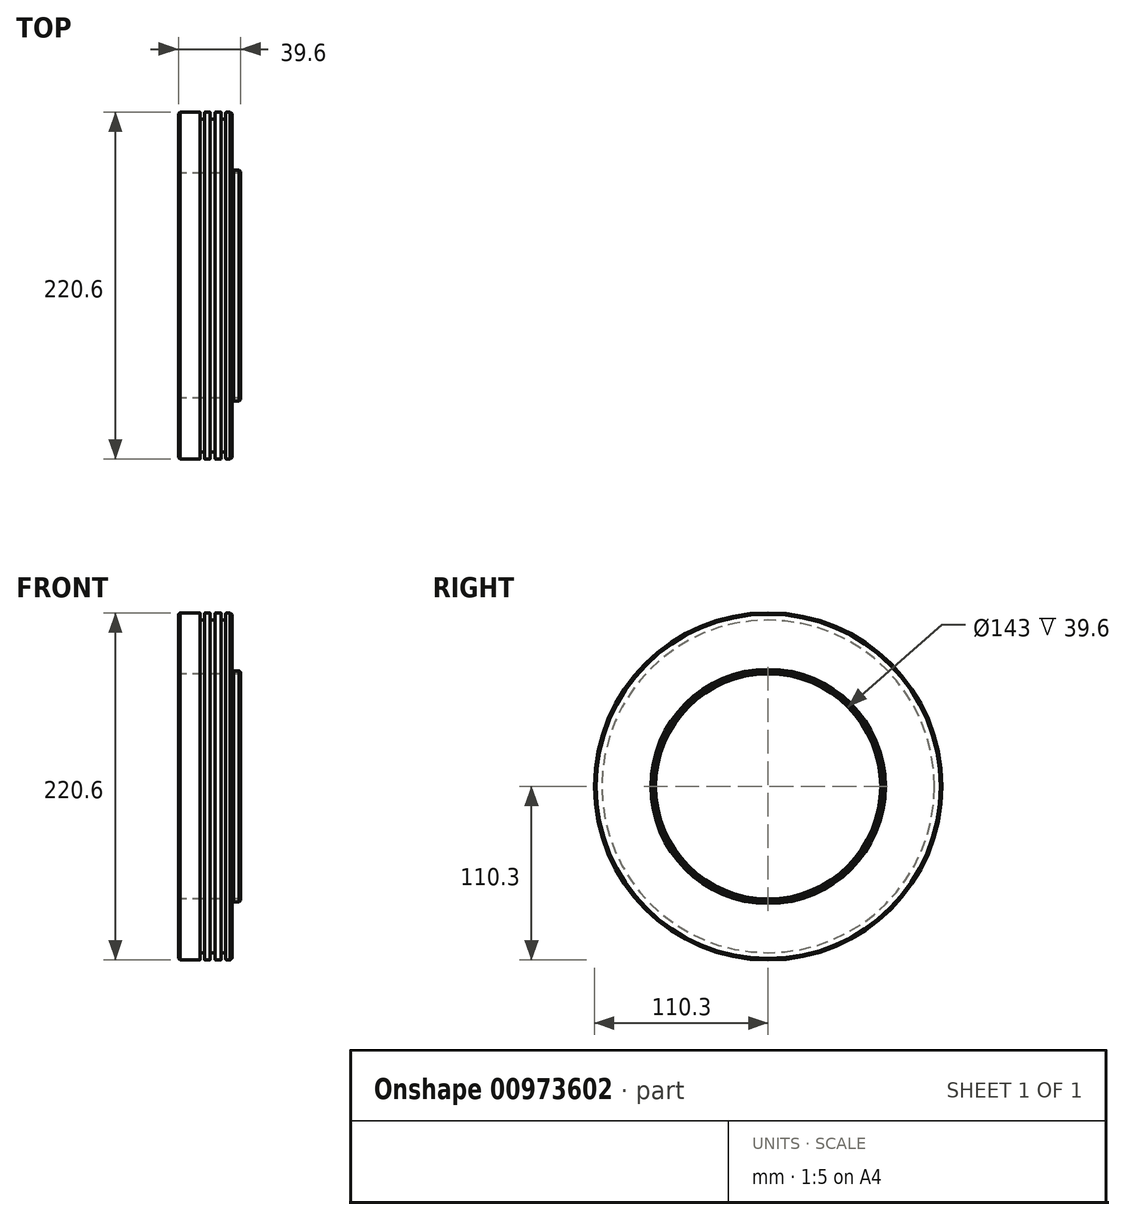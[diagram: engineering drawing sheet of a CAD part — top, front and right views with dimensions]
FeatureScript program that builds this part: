
annotation { "Feature Type Name" : "Feature", "Feature Type Description" : "" }
export const myFeature = defineFeature(function(context is Context, id is Id, definition is map)
    precondition{}
    {
        {
            var Q0;
            Q0=qCreatedBy(makeId("Front.planeOp"),FACE);
            var sketch = newSketch(context, id + "F0", { "sketchPlane" : qUnion([Q0])});
            skLineSegment(sketch, "E0.bottom", {"start": v(0, 0) * mm, "end": v(39.6, 0) * mm});
            skLineSegment(sketch, "E0.top", {"start": v(0, 38.8) * mm, "end": v(13.4, 38.8) * mm});
            skLineSegment(sketch, "E0.left", {"start": v(0, 0) * mm, "end": v(0, 38.8) * mm});
            skLineSegment(sketch, "E0.right", {"start": v(39.6, 0) * mm, "end": v(39.6, 1.92) * mm});
            skLineSegment(sketch, "E1", {"start": v(13.9, 38.3) * mm, "end": v(13.9, 34.62) * mm});
            skLineSegment(sketch, "E2", {"start": v(14.4, 34.12) * mm, "end": v(16.08, 34.12) * mm});
            skLineSegment(sketch, "E3", {"start": v(16.58, 34.62) * mm, "end": v(16.58, 38.3) * mm});
            skLineSegment(sketch, "E4", {"start": v(17.08, 38.8) * mm, "end": v(19.7, 38.8) * mm});
            skLineSegment(sketch, "E5", {"start": v(20.2, 38.3) * mm, "end": v(20.2, 34.62) * mm});
            skLineSegment(sketch, "E6", {"start": v(20.7, 34.12) * mm, "end": v(22.85, 34.12) * mm});
            skLineSegment(sketch, "E7", {"start": v(23.35, 34.62) * mm, "end": v(23.35, 38.3) * mm});
            skLineSegment(sketch, "E8", {"start": v(23.85, 38.8) * mm, "end": v(26.7, 38.8) * mm});
            skLineSegment(sketch, "E9", {"start": v(27.2, 38.3) * mm, "end": v(27.2, 34.62) * mm});
            skLineSegment(sketch, "E10", {"start": v(27.7, 34.12) * mm, "end": v(29.62, 34.12) * mm});
            skLineSegment(sketch, "E11", {"start": v(30.12, 34.62) * mm, "end": v(30.12, 38.3) * mm});
            skLineSegment(sketch, "E12", {"start": v(30.62, 38.8) * mm, "end": v(33.96, 38.8) * mm});
            skLineSegment(sketch, "E13", {"start": v(33.96, 38.8) * mm, "end": v(33.96, 1.92) * mm});
            skLineSegment(sketch, "E14", {"start": v(33.96, 1.92) * mm, "end": v(39.6, 1.92) * mm});
            skLineSegment(sketch, "E15.trimOffspring", {"start": v(30.12, 38.8) * mm, "end": v(33.96, 38.8) * mm});
            skLineSegment(sketch, "E16.trimOffspring", {"start": v(23.35, 38.8) * mm, "end": v(27.2, 38.8) * mm});
            skLineSegment(sketch, "E17.trimOffspring", {"start": v(16.58, 38.8) * mm, "end": v(20.2, 38.8) * mm});
            skLineSegment(sketch, "E18", {"start": v(0, -71.5) * mm, "end": v(42.38, -71.5) * mm, "construction": true});
            skPoint(sketch, "E19.visualSharp", {"position": v(13.9, 34.12) * mm});
            skArc(sketch, "E19.filletArc", {"start": v(13.9, 34.62) * mm, "mid": v(14.04, 34.26) * mm, "end": v(14.4, 34.12) * mm});
            skPoint(sketch, "E20.visualSharp", {"position": v(16.58, 34.12) * mm});
            skArc(sketch, "E20.filletArc", {"start": v(16.08, 34.12) * mm, "mid": v(16.44, 34.26) * mm, "end": v(16.58, 34.62) * mm});
            skPoint(sketch, "E21.visualSharp", {"position": v(16.58, 38.8) * mm});
            skArc(sketch, "E21.filletArc", {"start": v(17.08, 38.8) * mm, "mid": v(16.73, 38.65) * mm, "end": v(16.58, 38.3) * mm});
            skPoint(sketch, "E22.visualSharp", {"position": v(13.9, 38.8) * mm});
            skArc(sketch, "E22.filletArc", {"start": v(13.9, 38.3) * mm, "mid": v(13.75, 38.65) * mm, "end": v(13.4, 38.8) * mm});
            skPoint(sketch, "E23.visualSharp", {"position": v(20.2, 38.8) * mm});
            skArc(sketch, "E23.filletArc", {"start": v(20.2, 38.3) * mm, "mid": v(20.05, 38.65) * mm, "end": v(19.7, 38.8) * mm});
            skPoint(sketch, "E24.visualSharp", {"position": v(20.2, 34.12) * mm});
            skArc(sketch, "E24.filletArc", {"start": v(20.2, 34.62) * mm, "mid": v(20.34, 34.26) * mm, "end": v(20.7, 34.12) * mm});
            skPoint(sketch, "E25.visualSharp", {"position": v(23.35, 34.12) * mm});
            skArc(sketch, "E25.filletArc", {"start": v(22.85, 34.12) * mm, "mid": v(23.2, 34.26) * mm, "end": v(23.35, 34.62) * mm});
            skPoint(sketch, "E26.visualSharp", {"position": v(23.35, 38.8) * mm});
            skArc(sketch, "E26.filletArc", {"start": v(23.85, 38.8) * mm, "mid": v(23.5, 38.65) * mm, "end": v(23.35, 38.3) * mm});
            skPoint(sketch, "E27.visualSharp", {"position": v(27.2, 38.8) * mm});
            skArc(sketch, "E27.filletArc", {"start": v(27.2, 38.3) * mm, "mid": v(27.04, 38.65) * mm, "end": v(26.7, 38.8) * mm});
            skPoint(sketch, "E28.visualSharp", {"position": v(27.2, 34.12) * mm});
            skArc(sketch, "E28.filletArc", {"start": v(27.2, 34.62) * mm, "mid": v(27.34, 34.26) * mm, "end": v(27.7, 34.12) * mm});
            skPoint(sketch, "E29.visualSharp", {"position": v(30.12, 34.12) * mm});
            skArc(sketch, "E29.filletArc", {"start": v(29.62, 34.12) * mm, "mid": v(29.98, 34.26) * mm, "end": v(30.12, 34.62) * mm});
            skPoint(sketch, "E30.visualSharp", {"position": v(30.12, 38.8) * mm});
            skArc(sketch, "E30.filletArc", {"start": v(30.62, 38.8) * mm, "mid": v(30.27, 38.65) * mm, "end": v(30.12, 38.3) * mm});
            skSolve(sketch);
        }
        {
            var Q0;
            Q0=makeQuery(id+"F0.imprint","IMPRINT",FACE,{"disambiguationData":[TD([[makeQuery(id+"F0.imprint","IMPRINT",EDGE,{"derivedFrom":sQuery(id+"F0.wireOp",EDGE,"E0.bottom")}),1.0]])]});
            var Q1;
            Q1=sQuery(id+"F0.wireOp",EDGE,"E18");
            revolve(context, id + "F1", {"surfaceOperationType" : NewSurfaceOperationType.NEW, "entities" : qUnion([Q0]), "axis" : qUnion([Q1]), "revolveType" : RevolveType.FULL});
        }
        {
            var Q0;
            Q0=makeQuery(id+"F1.opRevolve","SWEPT_EDGE",EDGE,{"disambiguationData":[OSD([sQuery(id+"F0.wireOp",EDGE,"E0.top"),sQuery(id+"F0.wireOp",EDGE,"E0.left")])]});
            var Q1;
            Q1=makeQuery(id+"F1.opRevolve","SWEPT_EDGE",EDGE,{"disambiguationData":[OSD([sQuery(id+"F0.wireOp",EDGE,"E13"),sQuery(id+"F0.wireOp",EDGE,"E15.trimOffspring")])]});
            var Q2;
            Q2=makeQuery(id+"F1.opRevolve","SWEPT_EDGE",EDGE,{"disambiguationData":[OSD([sQuery(id+"F0.wireOp",EDGE,"E13"),sQuery(id+"F0.wireOp",EDGE,"E14")])]});
            var Q3;
            Q3=makeQuery(id+"F1.opRevolve","SWEPT_EDGE",EDGE,{"disambiguationData":[OSD([sQuery(id+"F0.wireOp",EDGE,"E0.right"),sQuery(id+"F0.wireOp",EDGE,"E14")])]});
            chamfer(context, id + "F2", {"entities" : qUnion([Q0, Q1, Q2, Q3]), "width" : 1 * mm, "tangentPropagation" : true});
        }
    });
